# Revit family: QF_HOSHIZAKI_HNC-120BE-R-B
name_source: partatom
category: Specialty Equipment
revit_build: Autodesk Revit 2016 (Build: 20150220_1215(x64)
units: mm (PartAtom-declared; Revit-internal decimal feet)

## family parameters
Always vertical = Yes
Cut with Voids When Loaded = No
OmniClass Number = 23.40.40.14
OmniClass Title = Food Service Equipment
Part Type = Normal
Room Calculation Point = No
Round Connector Dimension = Use Diameter
Shared = No
Work Plane-Based = No

## types (2) — shared parameters
Accessory = No
Apparent Power = 150 VA
Assembly Code = E1090320
Conn Conduit = No
Cycle = 50 Hz
Depth Actual = 345 mm  [stored 1.13189 ft]
Description = 42 LITRE SUSHI CASE, BLACK, RIGHT MOUNTED CONDENSER
Electric power = 150 W
FL Amps = 1 A
Height Actual = 270 mm  [stored 0.885827 ft]
Length Actual = 1200 mm
Manufacturer = HOSHIZAKI
Max Overcurrent Protection = 0 A
Min Ckt Ampacity = 0 A
Model = HNC-120BE-R-B
Number of Poles = 2
Phase = 1
URL = www.hoshizaki-europe.com
Weight = 32.00 kg
zero-valued in all types: Cost

## per-type parameters (varying)
| type | Volts |
| HNC-120BE-R-B_230V/1Ph/50Hz | 230 V |
| HNC-120BE-R-B_240V/1Ph/50Hz | 240 V |

note: [stored X ft] marks values corroborated as IEEE doubles in the binary element streams (Revit-internal decimal feet)

## geometry (parser evidence)
native form markers: Blend x6, Sweep x6
no freeform markers — native parametric forms only
